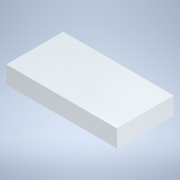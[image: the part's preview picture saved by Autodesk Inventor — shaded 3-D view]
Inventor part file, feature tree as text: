
AUTODESK INVENTOR PART (.ipt)
format: ipt  version: 2020 (Build 240168000, 168)  size: 96,768 bytes
history: native  units: mm
features: other x1, extrude x1, sketch x1
ambient origin geometry x8: Origin, YZ Plane, XZ Plane, XY Plane, X Axis, Y Axis, Z Axis, Center Point
bodies: Body1 (feature_tree)
feature tree (3):
  other  "Bryła1"
  extrude  "Wyciągnięcie proste1"  Depth=36.0mm
  sketch  "Szkic1"
